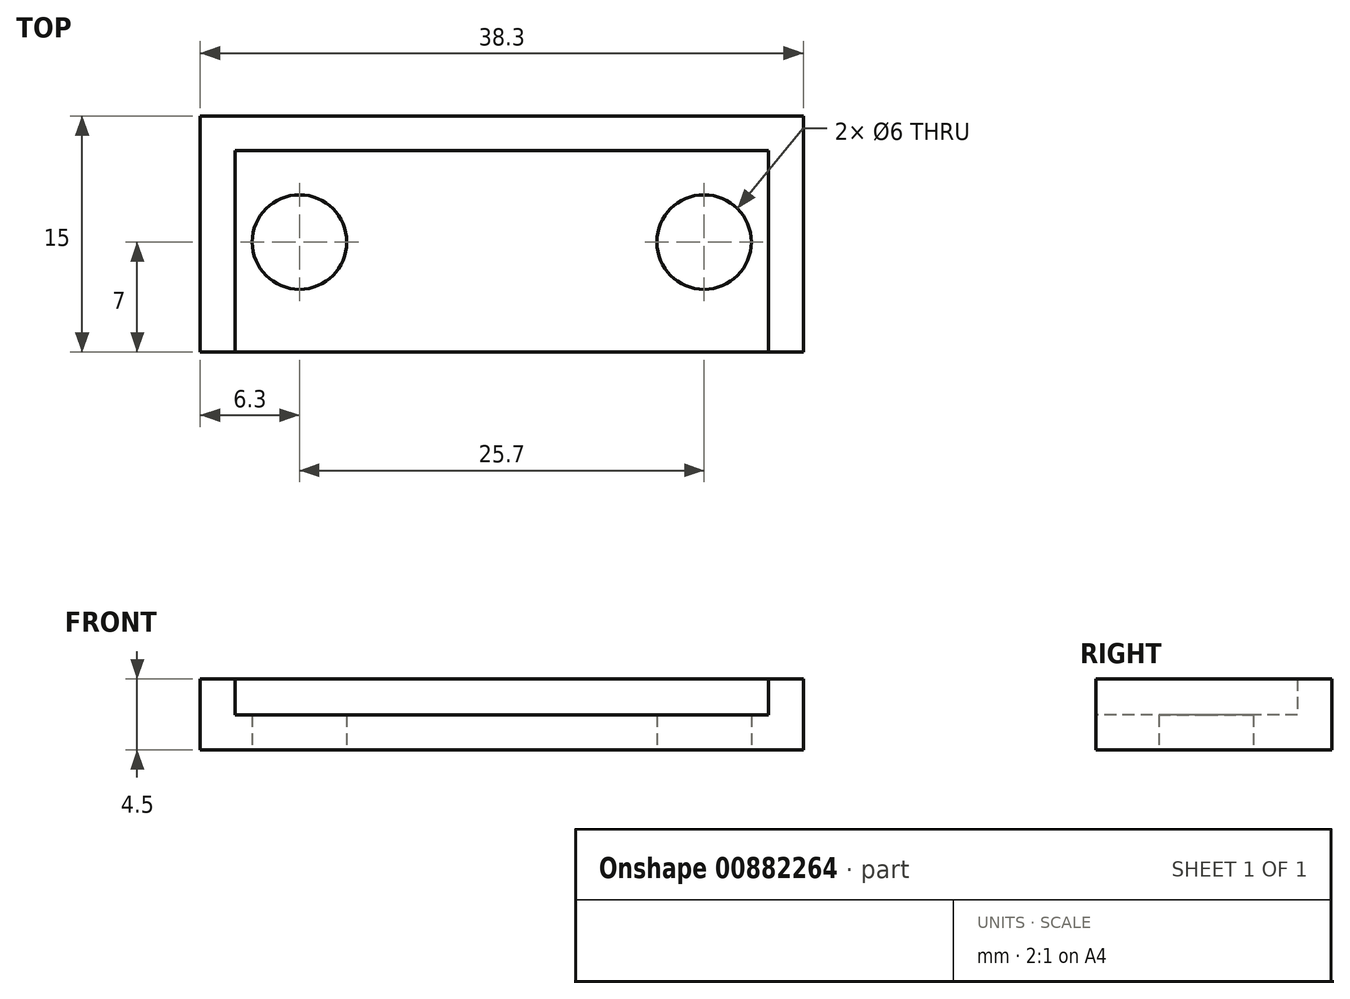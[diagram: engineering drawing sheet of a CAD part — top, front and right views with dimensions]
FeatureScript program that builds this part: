
annotation { "Feature Type Name" : "Feature", "Feature Type Description" : "" }
export const myFeature = defineFeature(function(context is Context, id is Id, definition is map)
    precondition{}
    {
        {
            var Q0;
            Q0=qCreatedBy(makeId("Top.planeOp"),FACE);
            var sketch = newSketch(context, id + "F0", { "sketchPlane" : qUnion([Q0])});
            skLineSegment(sketch, "E0.bottom", {"start": v(-38.3, 15) * mm, "end": v(0, 15) * mm});
            skLineSegment(sketch, "E0.top", {"start": v(-38.3, 0) * mm, "end": v(0, 0) * mm});
            skLineSegment(sketch, "E0.left", {"start": v(-38.3, 15) * mm, "end": v(-38.3, 0) * mm});
            skLineSegment(sketch, "E0.right", {"start": v(0, 15) * mm, "end": v(0, 0) * mm});
            skLineSegment(sketch, "E1.0", {"start": v(-38.3, 4) * mm, "end": v(0, 4) * mm, "construction": true});
            skLineSegment(sketch, "E2.0", {"start": v(-35, 15) * mm, "end": v(-35, 0) * mm, "construction": true});
            skLineSegment(sketch, "E3.0", {"start": v(-3.3, 15) * mm, "end": v(-3.3, 0) * mm, "construction": true});
            skLineSegment(sketch, "E4.0", {"start": v(-38.3, 7) * mm, "end": v(0, 7) * mm, "construction": true});
            skLineSegment(sketch, "E5.0", {"start": v(-32, 15) * mm, "end": v(-32, 0) * mm, "construction": true});
            skLineSegment(sketch, "E6.0", {"start": v(-6.3, 15) * mm, "end": v(-6.3, 0) * mm, "construction": true});
            skCircle(sketch, "E7", {"center": v(-32, 7) * mm, "radius": 3 * mm});
            skCircle(sketch, "E8", {"center": v(-6.3, 7) * mm, "radius": 3 * mm});
            skSolve(sketch);
        }
        {
            var Q0;
            Q0=makeQuery(id+"F0.imprint","IMPRINT",FACE,{"disambiguationData":[TD([[makeQuery(id+"F0.imprint","IMPRINT",EDGE,{"derivedFrom":sQuery(id+"F0.wireOp",EDGE,"E0.bottom")}),-1.0]])]});
            extrude(context, id + "F1", {"entities" : qUnion([Q0]), "depth" : 2.2 * mm, "offsetDistance" : 25 * mm});
        }
        {
            var Q0;
            Q0=makeQuery(id+"F1.opExtrude","CAP_FACE",FACE,{"disambiguationData":[OSD([sQuery(id+"F0.wireOp",EDGE,"E0.bottom"),sQuery(id+"F0.wireOp",EDGE,"E0.top"),sQuery(id+"F0.wireOp",EDGE,"E0.left"),sQuery(id+"F0.wireOp",EDGE,"E0.right"),sQuery(id+"F0.wireOp",EDGE,"E7"),sQuery(id+"F0.wireOp",EDGE,"E8")])],"isStart":false});
            var sketch = newSketch(context, id + "F2", { "sketchPlane" : qUnion([Q0])});
            skLineSegment(sketch, "E9.0", {"start": v(-38.3, 15) * mm, "end": v(-38.3, 0) * mm});
            skLineSegment(sketch, "E10.0", {"start": v(-38.3, 15) * mm, "end": v(0, 15) * mm});
            skLineSegment(sketch, "E11.0", {"start": v(0, 15) * mm, "end": v(0, 0) * mm});
            skLineSegment(sketch, "E12.0", {"start": v(-38.3, 0) * mm, "end": v(0, 0) * mm});
            skLineSegment(sketch, "E13.0", {"start": v(-36.1, 12.8) * mm, "end": v(-2.2, 12.8) * mm});
            skLineSegment(sketch, "E14.0", {"start": v(-36.1, 12.8) * mm, "end": v(-36.1, 0) * mm});
            skLineSegment(sketch, "E15.0", {"start": v(-2.2, 12.8) * mm, "end": v(-2.2, 0) * mm});
            skSolve(sketch);
        }
        {
            var Q0;
            Q0=makeQuery(id+"F2.imprint","IMPRINT",FACE,{"disambiguationData":[TD([[makeQuery(id+"F2.imprint","IMPRINT",EDGE,{"derivedFrom":sQuery(id+"F2.wireOp",EDGE,"E10.0")}),-1.0]])]});
            extrude(context, id + "F3", {"entities" : qUnion([Q0]), "operationType" : NewBodyOperationType.ADD, "depth" : 2.3 * mm, "offsetDistance" : 25 * mm});
        }
    });
